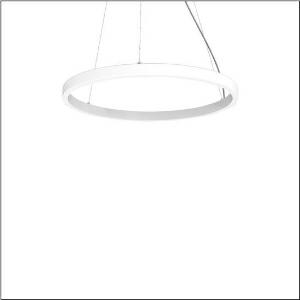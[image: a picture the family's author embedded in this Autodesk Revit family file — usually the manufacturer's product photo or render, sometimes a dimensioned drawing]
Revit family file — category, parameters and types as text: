
# Revit family: silica_21_ring-o_5pjbo3d1004a
name_source: partatom
category: Lighting Fixtures
units: mm (PartAtom-declared; Revit-internal decimal feet)

## family parameters
Cut with Voids When Loaded = No
Host = Face
Light Source = No
Part Type = Normal
Room Calculation Point = No
Round Connector Dimension = Use Diameter
Shared = No

## types (1)
- Silica 21 Ring-O (1 x LED, 6860 lm, 105 W, 3000K)
    Apparent Load = 105 VA
    CIE Flux Codes = 2 16 49 50 100
    Color Rendering = 80
    Color Temperature = 3000K
    Default Elevation = 1800 mm
    Description = Silica 21 Ring-O, suspended luminaire, of PMMA, frosted, light emission: outer ring side luminous distribution, primary light characteristic: symmetric, installation type: suspended mounting, LED, rated luminous flux: 6.860lm, luminous efficacy: 65lm/W, light colour: 830, colour temperature: 3000K, control gear: DALI 2, with terminal, 5-pole, mains connection: 230V, AC/DC, 0/50..60Hz, rated input power: 105W, housing, of extruded aluminium section, traffic white (RAL 9016), diameter: 1.100mm, ceiling canopy, traffic white (RAL 9016), protection rating (lamp compartment): IP40, insulation class (complete): insulation class I (protective earthing), certification: CE, impact resistance: IK02, permissible operating ambient temperature: 0..+35°C, packaging unit: 1 piece
    Height = 48 mm  [stored 0.15748 ft]
    Lamp = 1 x LED
    Lamp Light Flux = 6860 lm
    Lamp Power = 105 W
    Lamp count = 1
    Length = 1100 mm
    Luminous efficacy = 65 lm/W
    Manufacturer = Siteco
    ModVariant = No
    Model = 5PJBO3D1004A
    Mounting Place = Ceiling
    Mounting Type = Pendant
    Number of Poles = 1
    OnlyDefault = Yes
    Power Factor = 1
    Product Name = Silica 21 Ring-O
    Product group = suspended luminaire
    ProductGroupID = 904
    Protection Class = Protection class I
    Protection Degree = IP 40
    RLX_Detail_Level = 1
    RLX_Emergency_Light_Flux = 0 lm
    RLX_Emergency_Type = 0
    RLX_Emergency_Type_DB = No
    RlxData = <blob elided: 13525 chars, md5=bd245054>
    Socket = socket
    Standby Power = 0 W
    System Light Flux = 6860 lm
    System Power = 105 W
    Type Comments = Product without accessories
    Type Image = l_1258387.jpg
    URL = http://relux.com
    VarID = ---
    Voltage = 0 V
    Weight = 0.00 kg
    Width = 0 mm  [stored 0 ft]

note: [stored X ft] marks values corroborated as IEEE doubles in the binary element streams (Revit-internal decimal feet)

## geometry (parser evidence)
native form markers: Sweep x11
no freeform markers — native parametric forms only
